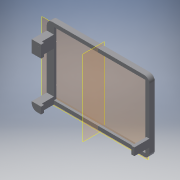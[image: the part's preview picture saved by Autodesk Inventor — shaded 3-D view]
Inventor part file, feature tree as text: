
AUTODESK INVENTOR PART (.ipt)
format: ipt  version: 2019.4 (Build 234330000, 330)  size: 278,528 bytes
history: native  units: mm
features: extrude x6, sketch x6, projected_geometry x6, reference x5, other x5, plane x2
ambient origin geometry x8: Origin, YZ Plane, XZ Plane, XY Plane, X Axis, Y Axis, Z Axis, Center Point
bodies: Solid1 (feature_tree)
feature tree (30):
  plane  "Work Plane1"
  extrude  "Extrusion1"  Depth=1.0mm
  extrude  "Extrusion2"  Depth=1.0mm
  extrude  "Extrusion3"  Depth=4.0mm TaperAngle=0.0deg
  plane  "Work Plane2"
  extrude  "Extrusion4"  Depth=20.0mm
  extrude  "Extrusion5"  Depth=2.0mm
  extrude  "Extrusion6"  Depth=4.0mm
  sketch  "Sketch1"  dims[d0=4.0mm d1=1.0mm]
  reference  "Reference1"
  reference  "Reference2"
  sketch  "Sketch2"  dims[d2=3.0mm d3=0.0mm d4=1.0mm]
  reference  "Reference3"
  projected_geometry  "Projected Loop1"
  sketch  "Sketch3"  dims[d5=0.5mm d6=4.0mm d7=0.0mm]
  projected_geometry  "Projected Loop2"
  sketch  "Sketch4"  dims[d8=20.0mm d9=0.0mm d10=2.0mm]
  projected_geometry  "Projected Loop3"
  reference  "Reference4"
  reference  "Reference5"
  sketch  "Sketch5"  dims[d11=2.0mm d12=2.0mm]
  projected_geometry  "Projected Loop4"
  sketch  "Sketch6"  dims[d13=2.0mm d14=4.0mm d15=10.0mm d20=16.0mm d21=16.0mm d22=0.0mm d23=14.0mm d24=2.8mm d25=2.8mm d26=16.0mm d27=0.0mm d28=13.5mm d29=9.0mm d30=9.0mm d31=3.0mm d32=16.0mm d33=0.0mm]
  projected_geometry  "Projected Loop5"
  projected_geometry  "Projected Loop6"
  other  "Full_HITscope_v0.iam"
  other  "00_24wellplate_base_2:1"
  other  "03_Omniscope_lid_lenses:1"
  other  "00_Microlinearmotor:2"
  other  "00_Microlinearmotor:1"
